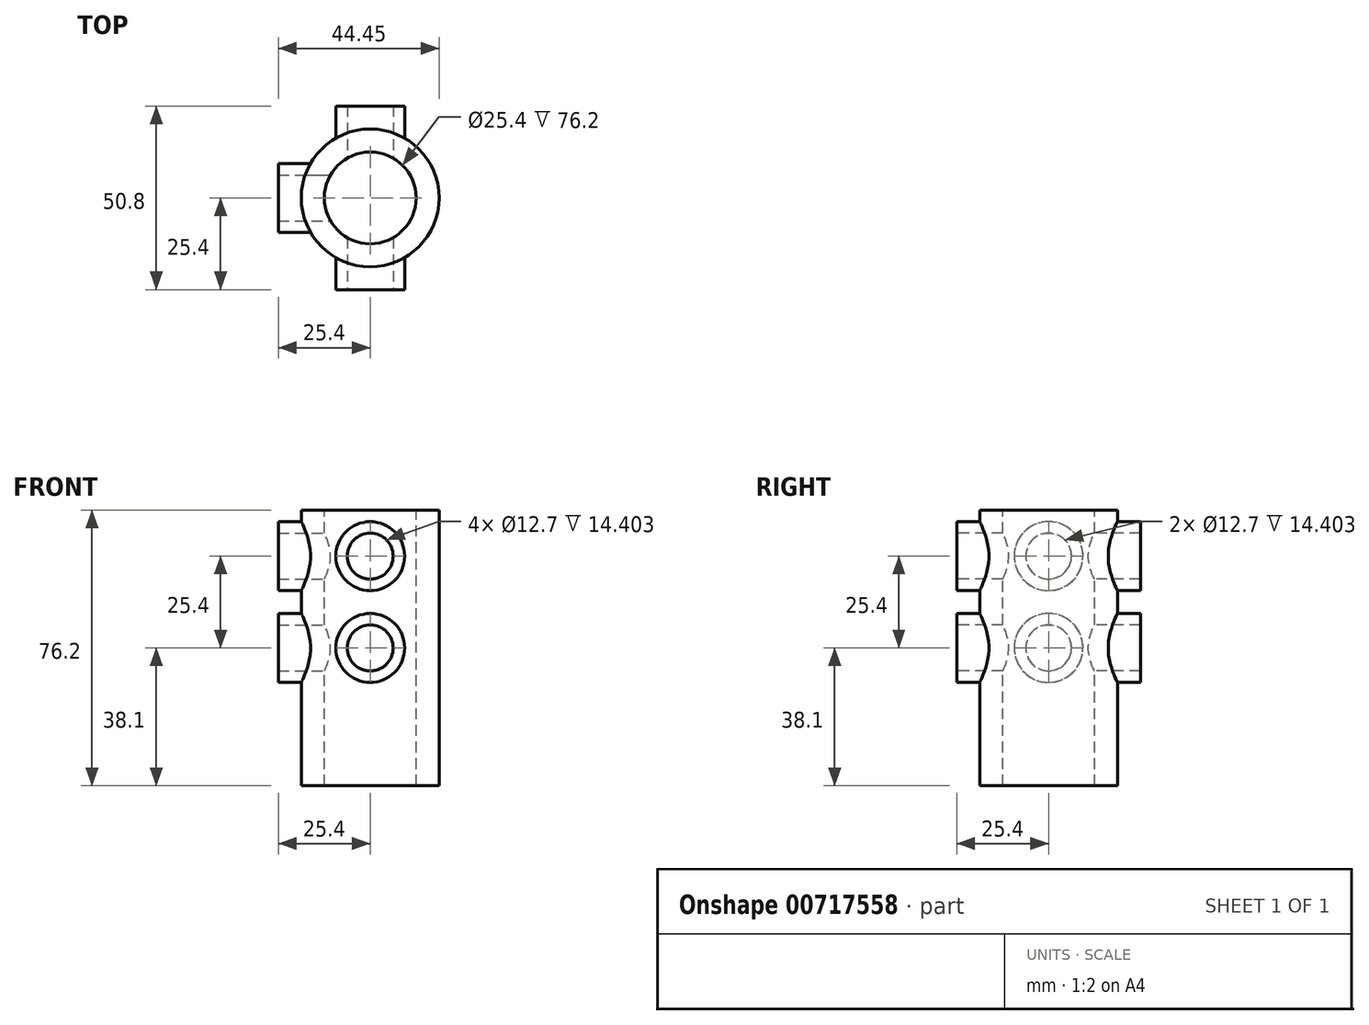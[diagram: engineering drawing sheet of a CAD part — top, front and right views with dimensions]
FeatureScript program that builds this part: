
annotation { "Feature Type Name" : "Feature", "Feature Type Description" : "" }
export const myFeature = defineFeature(function(context is Context, id is Id, definition is map)
    precondition{}
    {
        {
            var Q0;
            Q0=qCreatedBy(makeId("Top.planeOp"),FACE);
            var sketch = newSketch(context, id + "F0", { "sketchPlane" : qUnion([Q0])});
            skCircle(sketch, "E0", {"center": v(0, 0) * mm, "radius": 19.05 * mm});
            skSolve(sketch);
        }
        {
            var Q0;
            Q0 = qSketchRegion(id + "F0", true);
            extrude(context, id + "F1", {"entities" : qUnion([Q0]), "depth" : 76.2 * mm, "offsetDistance" : 25.4 * mm});
        }
        {
            var Q0;
            Q0=qCreatedBy(makeId("Front.planeOp"),FACE);
            var sketch = newSketch(context, id + "F2", { "sketchPlane" : qUnion([Q0])});
            skCircle(sketch, "E1", {"center": v(0, 63.5) * mm, "radius": 9.53 * mm});
            skCircle(sketch, "E2", {"center": v(0, 38.1) * mm, "radius": 9.53 * mm});
            skSolve(sketch);
        }
        {
            var Q0;
            Q0 = qSketchRegion(id + "F2", true);
            extrude(context, id + "F3", {"entities" : qUnion([Q0]), "operationType" : NewBodyOperationType.ADD, "endBound" : BoundingType.SYMMETRIC, "oppositeDirection" : true, "depth" : 50.8 * mm, "offsetDistance" : 25.4 * mm});
        }
        {
            var Q0;
            Q0=qCreatedBy(makeId("Right.planeOp"),FACE);
            var sketch = newSketch(context, id + "F4", { "sketchPlane" : qUnion([Q0])});
            skCircle(sketch, "E3", {"center": v(0, 63.5) * mm, "radius": 9.53 * mm});
            skCircle(sketch, "E4", {"center": v(0, 38.1) * mm, "radius": 9.53 * mm});
            skSolve(sketch);
        }
        {
            var Q0;
            Q0 = qSketchRegion(id + "F4", true);
            extrude(context, id + "F5", {"entities" : qUnion([Q0]), "operationType" : NewBodyOperationType.ADD, "oppositeDirection" : true, "depth" : 25.4 * mm, "offsetDistance" : 25.4 * mm});
        }
        {
            var Q0;
            Q0=qCreatedBy(makeId("Right.planeOp"),FACE);
            var sketch = newSketch(context, id + "F6", { "sketchPlane" : qUnion([Q0])});
            skCircle(sketch, "E5", {"center": v(0, 63.5) * mm, "radius": 6.35 * mm});
            skCircle(sketch, "E6", {"center": v(0, 38.1) * mm, "radius": 6.35 * mm});
            skSolve(sketch);
        }
        {
            var Q0;
            Q0 = qSketchRegion(id + "F6", true);
            extrude(context, id + "F7", {"entities" : qUnion([Q0]), "operationType" : NewBodyOperationType.REMOVE, "oppositeDirection" : true, "depth" : 30.48 * mm, "offsetDistance" : 25.4 * mm});
        }
        {
            var Q0;
            Q0=makeQuery(id+"F3.opExtrude","CAP_FACE",FACE,{"disambiguationData":[OSD([sQuery(id+"F2.wireOp",EDGE,"E1")])],"isStart":true});
            var sketch = newSketch(context, id + "F8", { "sketchPlane" : qUnion([Q0])});
            skCircle(sketch, "E7", {"center": v(0, 63.5) * mm, "radius": 6.35 * mm});
            skCircle(sketch, "E8", {"center": v(0, 38.1) * mm, "radius": 6.35 * mm});
            skSolve(sketch);
        }
        {
            var Q0;
            Q0 = qSketchRegion(id + "F8", true);
            extrude(context, id + "F9", {"entities" : qUnion([Q0]), "operationType" : NewBodyOperationType.REMOVE, "endBound" : BoundingType.THROUGH_ALL, "oppositeDirection" : true, "depth" : 25.4 * mm, "offsetDistance" : 25.4 * mm});
        }
        {
            var Q0;
            Q0=makeQuery(id+"F1.opExtrude","CAP_FACE",FACE,{"disambiguationData":[OSD([sQuery(id+"F0.wireOp",EDGE,"E0")])],"isStart":false});
            var sketch = newSketch(context, id + "F10", { "sketchPlane" : qUnion([Q0])});
            skCircle(sketch, "E9", {"center": v(0, 0) * mm, "radius": 12.7 * mm});
            skSolve(sketch);
        }
        {
            var Q0;
            Q0 = qSketchRegion(id + "F10", true);
            extrude(context, id + "F11", {"entities" : qUnion([Q0]), "operationType" : NewBodyOperationType.REMOVE, "endBound" : BoundingType.THROUGH_ALL, "oppositeDirection" : true, "depth" : 25.4 * mm, "offsetDistance" : 25.4 * mm});
        }
    });
